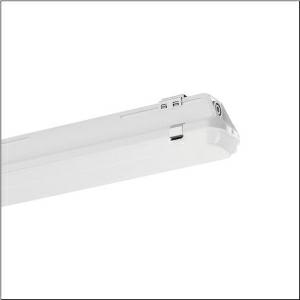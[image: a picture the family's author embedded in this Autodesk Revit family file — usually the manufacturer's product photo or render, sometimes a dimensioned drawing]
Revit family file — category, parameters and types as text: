
# Revit family: monsun_r__11_51fp207p460h_8ebd
name_source: partatom
category: Lighting Fixtures
units: mm (PartAtom-declared; Revit-internal decimal feet)

## family parameters
Cut with Voids When Loaded = No
Host = Face
Light Source = No
Part Type = Normal
Room Calculation Point = No
Round Connector Dimension = Use Diameter
Shared = No

## types (1)
- Monsun® 11 (1 x LED, 6030 lm, 37.7 W, 4000K)
    Apparent Load = 38 VA
    CIE Flux Codes = 45 75 93 94 100
    Color Rendering = 80
    Color Temperature = 4000K
    Default Elevation = 1800 mm
    Description = Monsun® 11, damp-proof luminaire, chain hanger, primary optical cover: enclosure, of PC, light emission: direct distribution, primary light characteristic: symmetric, installation type: suspended mounting, surface-mounted, horizontal mounting, vertical mounting, LED, rated luminous flux: 6.030lm, luminous efficacy: 160lm/W, light colour: 840, colour temperature: 4000K, control gear: ON/OFF, with terminal, 3-pole, max. 2.5mm², mains connection: 220..240V, AC, 50/60Hz, rated input power: 38W, luminaire housing, of glass-fibre reinforced polyester, uncoated, bright grey, incl. chain hanger, length: 1.590mm, width: 90mm, height: 88mm, clip for enclosure, of stainless steel (V2A), ceiling mounting element, of stainless steel (V2A), chain hanger, of stainless steel (V2A), protection rating (complete): IP66, insulation class (complete): insulation class I (protective earthing), certification: CE, ENEC, VDE, UKCA, protection symbol: D, impact resistance: IK08, permissible operating ambient temperature: -35..+40°C, standard: EN 50419, EN 60598-2-1, no direct snow, no direct sun, no direct rain, for indoor or canopied outdoor use, corresponds to IFS (International Featured Standards) requirements for safety and quality in the food industry, contact your sales advisor before using the luminaires in applications with unclear chemical exposure, large temperature fluctuations or condensation-forming humidity, LABS conformity tested according to VDMA 24364:2018-05, packaging unit: 1 piece
    Height = 89 mm
    Lamp = 1 x LED
    Lamp Light Flux = 6030 lm
    Lamp Power = 37.7 W
    Lamp count = 1
    Length = 1590 mm
    Luminous efficacy = 160 lm/W
    Manufacturer = Siteco
    ModVariant = No
    Model = 51FP207P460H
    Mounting Place = Ceiling
    Mounting Type = Surface mounted
    Number of Poles = 1
    OnlyDefault = Yes
    Power Factor = 1
    Product Name = Monsun® 11
    Product group = damp-proof luminaire
    ProductGroupID = 300
    Protection Class = Protection class I
    Protection Degree = IP 66
    RLX_Detail_Level = 1
    RLX_Emergency_Light_Flux = 0 lm
    RLX_Emergency_Type = 0
    RLX_Emergency_Type_DB = No
    RlxData = <blob elided: 88665 chars, md5=c009333e>
    Socket = socket
    Standby Power = 0 W
    System Light Flux = 6030 lm
    System Power = 38 W
    Type Comments = Product without accessories
    Type Image = l_1349237.jpg
    URL = http://relux.com
    VarID = ---
    Voltage = 0 V
    Weight = 0.00 kg
    Width = 90 mm

## geometry (parser evidence)
native form markers: Blend x4, Sweep x11
no freeform markers — native parametric forms only
